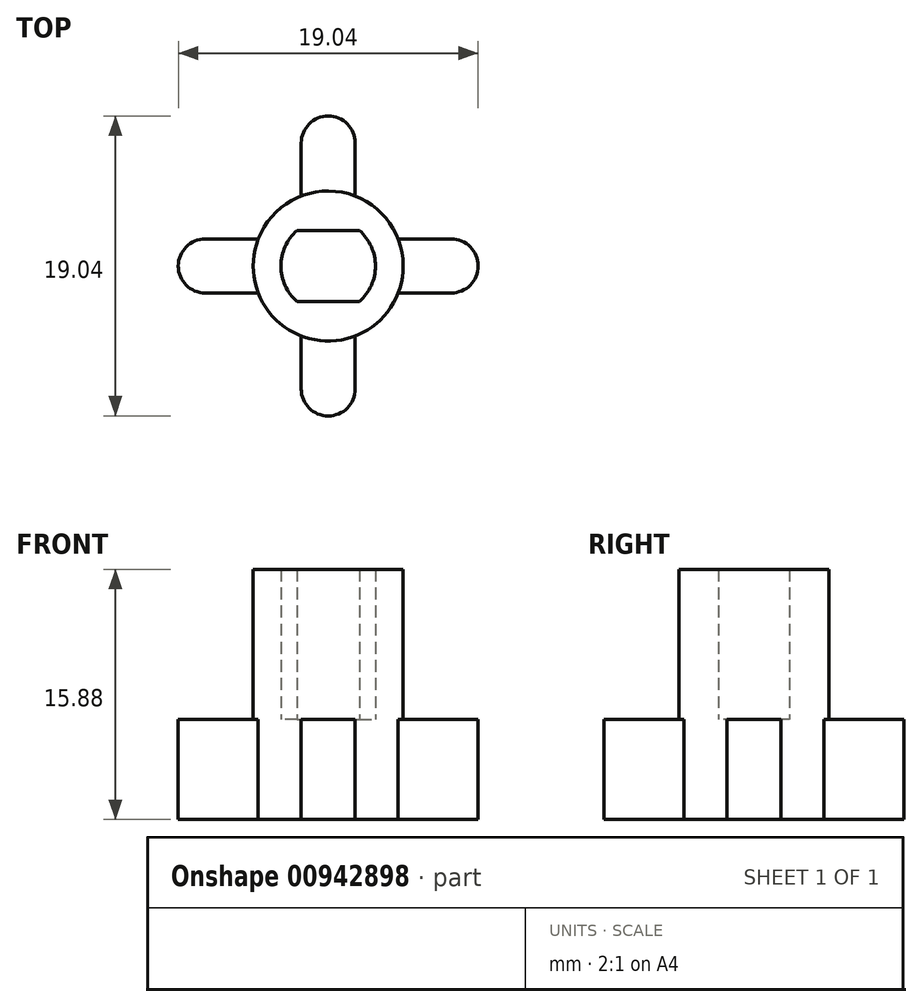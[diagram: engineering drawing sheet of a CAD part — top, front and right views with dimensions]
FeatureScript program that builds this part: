
annotation { "Feature Type Name" : "Feature", "Feature Type Description" : "" }
export const myFeature = defineFeature(function(context is Context, id is Id, definition is map)
    precondition{}
    {
        {
            var Q0;
            Q0=qCreatedBy(makeId("Top.planeOp"),FACE);
            var sketch = newSketch(context, id + "F0", { "sketchPlane" : qUnion([Q0])});
            skCircle(sketch, "E0", {"center": v(0, 0) * mm, "radius": 4.76 * mm});
            skSolve(sketch);
        }
        {
            var Q0;
            Q0=qSketchRegion(id+"F0",true);
            extrude(context, id + "F1", {"entities" : qUnion([Q0]), "depth" : 9.52 * mm, "offsetDistance" : 25.4 * mm, "hasSecondDirection" : true, "secondDirectionOppositeDirection" : true, "secondDirectionDepth" : 6.35 * mm});
        }
        {
            var Q0;
            Q0=qCreatedBy(makeId("Top.planeOp"),FACE);
            var sketch = newSketch(context, id + "F2", { "sketchPlane" : qUnion([Q0])});
            skCircle(sketch, "E1", {"center": v(0, 0) * mm, "radius": 3 * mm});
            skLineSegment(sketch, "E2", {"start": v(-1.98, 2.25) * mm, "end": v(1.98, 2.25) * mm});
            skLineSegment(sketch, "E3", {"start": v(-1.98, -2.25) * mm, "end": v(1.98, -2.25) * mm});
            skSolve(sketch);
        }
        {
            var Q0;
            Q0=qCreatedBy(makeId("Top.planeOp"),FACE);
            var sketch = newSketch(context, id + "F3", { "sketchPlane" : qUnion([Q0])});
            skCircle(sketch, "E4", {"center": v(0, 0) * mm, "radius": 2.5 * mm});
            skSolve(sketch);
        }
        {
            var Q0;
            {var subQ0=sQuery(id+"F2.wireOp",EDGE,"E2");Q0=makeQuery(id+"F2.imprint","IMPRINT",FACE,{"disambiguationData":[TD([[makeQuery(id+"F2.imprint","IMPRINT",EDGE,{"derivedFrom":subQ0}),-1.0]])]});}
            extrude(context, id + "F4", {"entities" : qUnion([Q0]), "operationType" : NewBodyOperationType.REMOVE, "endBound" : BoundingType.THROUGH_ALL, "depth" : 25.4 * mm, "offsetDistance" : 25.4 * mm});
        }
        {
            var Q0;
            Q0=qCreatedBy(makeId("Top.planeOp"),FACE);
            var sketch = newSketch(context, id + "F5", { "sketchPlane" : qUnion([Q0])});
            skCircle(sketch, "E5", {"center": v(-7.81, 0) * mm, "radius": 1.71 * mm, "construction": true});
            skLineSegment(sketch, "E6", {"start": v(0, 5.16) * mm, "end": v(0, -5.29) * mm, "construction": true});
            skLineSegment(sketch, "E7", {"start": v(-7.81, 1.71) * mm, "end": v(0, 1.71) * mm});
            skLineSegment(sketch, "E8", {"start": v(-7.81, -1.71) * mm, "end": v(0, -1.71) * mm});
            skArc(sketch, "E9", {"start": v(-7.81, 1.71) * mm, "mid": v(-9.53, 0) * mm, "end": v(-7.81, -1.71) * mm});
            skLineSegment(sketch, "E10", {"start": v(0, -1.71) * mm, "end": v(0, 1.71) * mm});
            skSolve(sketch);
        }
        {
            var Q0;
            Q0 = qSketchRegion(id + "F5", true);
            var Q1;
            Q1=makeQuery(id+"F1.opExtrude","CAP_FACE",FACE,{"disambiguationData":[OSD([sQuery(id+"F0.wireOp",EDGE,"E0")])],"isStart":true});
            extrude(context, id + "F6", {"entities" : qUnion([Q0]), "endBound" : BoundingType.UP_TO_SURFACE, "oppositeDirection" : true, "depth" : 25.4 * mm, "endBoundEntityFace" : qUnion([Q1]), "offsetDistance" : 25.4 * mm});
        }
        {
            var Q0;
            Q0=makeQuery(id+"F6.opExtrude","SWEPT_BODY",BODY,{"disambiguationData":[OSD([sQuery(id+"F5.wireOp",EDGE,"E7"),sQuery(id+"F5.wireOp",EDGE,"E8"),sQuery(id+"F5.wireOp",EDGE,"E9"),sQuery(id+"F5.wireOp",EDGE,"E10")])]});
            var Q1;
            Q1=makeQuery(id+"F1.opExtrude","SWEPT_FACE",FACE,{"disambiguationData":[OSD([sQuery(id+"F0.wireOp",EDGE,"E0")])]});
            circularPattern(context, id + "F7", {"operationType" : NewBodyOperationType.ADD, "entities" : qUnion([Q0]), "axis" : qUnion([Q1]), "angle" : 360 * degree, "instanceCount" : 4, "equalSpace" : true});
        }
    });
